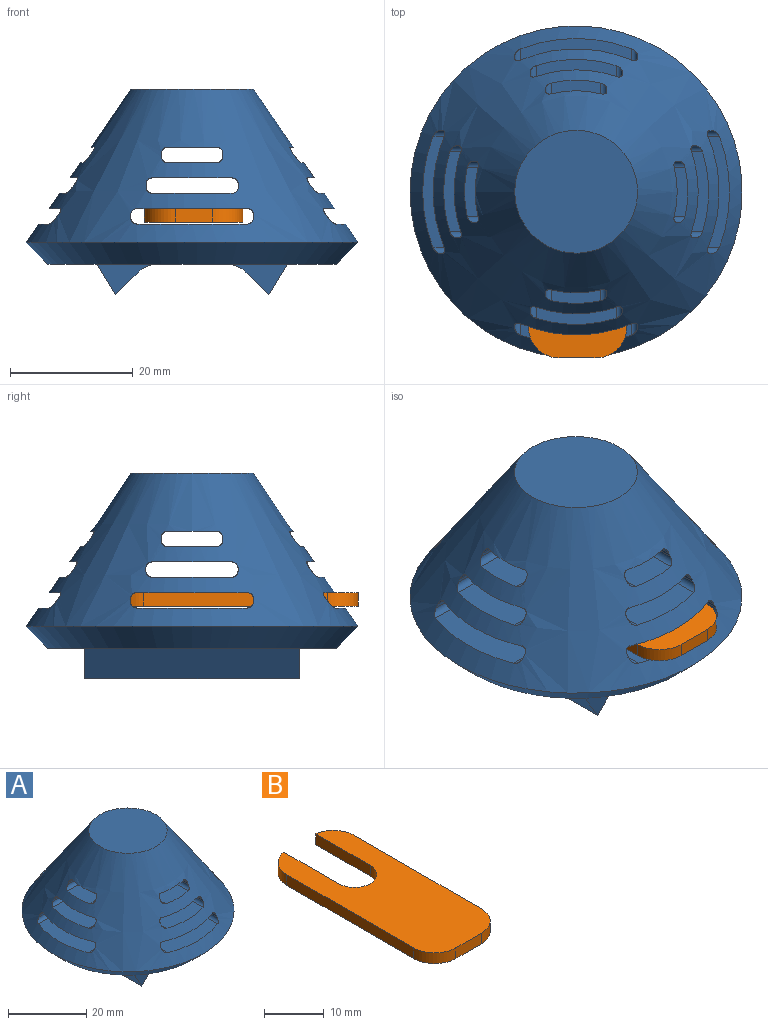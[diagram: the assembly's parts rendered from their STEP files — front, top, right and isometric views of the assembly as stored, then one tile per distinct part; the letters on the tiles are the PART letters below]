
ASSEMBLY  parts=2 mates=1
PART A: 97 faces, bbox 54.1x54.1x33.5 mm
  f0: cone r=27.04mm half-angle=34.3deg, axis (0,0,-1), area 2971.5mm2, adj f1,f2,f3,f4,f5,f6,f7,f8
  f1: cylinder r=1mm len=12.4mm, axis (0,-1,0), area 18.3mm2, adj f0,f24,f30,f66
  f2: cylinder r=1mm len=13.72mm, axis (0,-1,0), area 20mm2, adj f0,f27,f30,f64
  f3: cylinder r=1mm len=13.72mm, axis (0,-1,0), area 20mm2, adj f0,f27,f31,f67
  f4: cylinder r=1mm len=12.4mm, axis (0,-1,0), area 18.3mm2, adj f0,f24,f31,f69
  f5: plane 11.75x0.5mm, normal (1,0,0), area 5.8mm2, adj f0,f25,f26,f62
  f6: plane 11.75x0.5mm, normal (-1,0,0), area 5.8mm2, adj f0,f28,f29,f72
  f7: cylinder r=1mm len=12.64mm, axis (0,-1,0), area 18.8mm2, adj f0,f33,f36,f93
  f8: plane 12x0.5mm, normal (1,0,0), area 5.9mm2, adj f0,f35,f37,f95
  f9: cylinder r=1mm len=14.07mm, axis (0,-1,0), area 20.5mm2, adj f0,f34,f36,f91
  f10: cylinder r=1mm len=14.07mm, axis (0,-1,0), area 20.5mm2, adj f0,f34,f39,f87
  f11: plane 12x0.5mm, normal (-1,0,0), area 5.9mm2, adj f0,f38,f40,f89
  f12: cylinder r=1mm len=12.64mm, axis (0,-1,0), area 18.8mm2, adj f0,f33,f39,f85
  f13: cylinder r=1mm len=12.78mm, axis (0,-1,0), area 19mm2, adj f0,f41,f44,f81
  f14: plane 12.15x0.5mm, normal (1,0,0), area 6mm2, adj f0,f43,f45,f83
  f15: cylinder r=1mm len=14.31mm, axis (0,-1,0), area 20.8mm2, adj f0,f42,f44,f79
  f16: cylinder r=1mm len=14.31mm, axis (0,-1,0), area 20.8mm2, adj f0,f42,f47,f75
  f17: plane 12.15x0.5mm, normal (-1,0,0), area 6mm2, adj f0,f46,f48,f77
  f18: cylinder r=1mm len=12.78mm, axis (0,-1,0), area 19mm2, adj f0,f41,f47,f73
  f19: cone r=5mm half-angle=2deg, axis (0,0,-1), area 197.3mm2, adj f24,f49
  f20: plane 47x47mm, normal (0,0,-1), area 951.4mm2, adj f21,f23,f51,f53,f54,f55,f57,f58
  f21: cone r=5mm half-angle=2deg, axis (0,0,-1), area 200.8mm2, adj f20,f42
  f22: plane 20x20mm, normal (0,0,1), area 314.2mm2, adj f0
  f23: cone r=23.5mm half-angle=45deg, axis (0,0,1), area 793.8mm2, adj f0,f20
  f24: plane 32.92x32.92mm, normal (0,0,-1), area 398.4mm2, adj f0,f1,f4,f19,f25,f29,f65,f66
  f25: cylinder r=1mm len=12.4mm, axis (0,-1,0), area 18.3mm2, adj f0,f5,f24,f65
  f26: cylinder r=1mm len=13.72mm, axis (0,-1,0), area 20mm2, adj f0,f5,f27,f63
  f27: plane 36.33x36.33mm, normal (0,0,1), area 451.1mm2, adj f0,f2,f3,f26,f28,f32,f63,f64
  f28: cylinder r=1mm len=13.72mm, axis (0,-1,0), area 20mm2, adj f0,f6,f27,f68
  f29: cylinder r=1mm len=12.4mm, axis (0,-1,0), area 18.3mm2, adj f0,f6,f24,f70
  f30: plane 11.75x0.5mm, normal (1,0,0), area 5.8mm2, adj f0,f1,f2,f61
  f31: plane 11.75x0.5mm, normal (-1,0,0), area 5.8mm2, adj f0,f3,f4,f71
  f32: cone r=5mm half-angle=2deg, axis (0,0,-1), area 70.2mm2, adj f27,f33
  f33: plane 39.74x39.74mm, normal (0,0,-1), area 781.6mm2, adj f0,f7,f12,f32,f35,f40,f85,f88
  f34: plane 43.15x43.15mm, normal (0,0,1), area 869.4mm2, adj f0,f9,f10,f37,f38,f50,f87,f90
  f35: cylinder r=1mm len=12.64mm, axis (0,-1,0), area 18.8mm2, adj f0,f8,f33,f96
  f36: plane 12x0.5mm, normal (1,0,0), area 5.9mm2, adj f0,f7,f9,f94
  f37: cylinder r=1mm len=14.07mm, axis (0,-1,0), area 20.5mm2, adj f0,f8,f34,f92
  f38: cylinder r=1mm len=14.07mm, axis (0,-1,0), area 20.5mm2, adj f0,f11,f34,f90
  f39: plane 12x0.5mm, normal (-1,0,0), area 5.9mm2, adj f0,f10,f12,f86
  f40: cylinder r=1mm len=12.64mm, axis (0,-1,0), area 18.8mm2, adj f0,f11,f33,f88
  f41: plane 46.56x46.56mm, normal (0,0,-1), area 1240.7mm2, adj f0,f13,f18,f43,f48,f50,f73,f76
  f42: plane 49.98x49.98mm, normal (0,0,1), area 1363.9mm2, adj f0,f15,f16,f21,f45,f46,f75,f78
  f43: cylinder r=1mm len=12.78mm, axis (0,-1,0), area 19mm2, adj f0,f14,f41,f84
  f44: plane 12.15x0.5mm, normal (1,0,0), area 6mm2, adj f0,f13,f15,f82
  f45: cylinder r=1mm len=14.31mm, axis (0,-1,0), area 20.8mm2, adj f0,f14,f42,f80
  f46: cylinder r=1mm len=14.31mm, axis (0,-1,0), area 20.8mm2, adj f0,f17,f42,f78
  f47: plane 12.15x0.5mm, normal (-1,0,0), area 6mm2, adj f0,f16,f18,f74
  f48: cylinder r=1mm len=12.78mm, axis (0,-1,0), area 19mm2, adj f0,f17,f41,f76
  f49: plane 8.15x8.15mm, normal (0,0,-1), area 52.2mm2, adj f19
  f50: cone r=5mm half-angle=2deg, axis (0,0,-1), area 72.9mm2, adj f34,f41
  f51: plane 35x5mm, normal (-0.86,0,-0.51), area 204.1mm2, adj f20,f52,f53,f54
  f52: plane 35x3.54mm, normal (0.71,0,-0.71), area 175mm2, adj f51,f53,f54,f60
  f53: plane 10.07x5mm, normal (0,-1,0), area 20.5mm2, adj f20,f51,f52,f60
  f54: plane 10.07x5mm, normal (0,1,0), area 20.5mm2, adj f20,f51,f52,f60
  f55: plane 35x5mm, normal (0.86,0,-0.51), area 204.1mm2, adj f20,f56,f57,f58
  f56: plane 35x3.54mm, normal (-0.71,0,-0.71), area 175mm2, adj f55,f57,f58,f59
  f57: plane 10.07x5mm, normal (0,-1,0), area 20.5mm2, adj f20,f55,f56,f59
  f58: plane 10.07x5mm, normal (0,1,0), area 20.5mm2, adj f20,f55,f56,f59
  f59: cylinder r=5mm len=35mm, axis (0,-1,0), area 137.4mm2, adj f20,f56,f57,f58
  f60: cylinder r=5mm len=35mm, axis (0,1,0), area 137.4mm2, adj f20,f52,f53,f54
  f61: plane 11.75x0.5mm, normal (0,1,0), area 5.8mm2, adj f0,f30,f64,f66
  f62: plane 11.75x0.5mm, normal (0,-1,0), area 5.8mm2, adj f0,f5,f63,f65
  f63: cylinder r=1mm len=13.72mm, axis (1,0,0), area 20mm2, adj f0,f26,f27,f62
  f64: cylinder r=1mm len=13.72mm, axis (1,0,0), area 20mm2, adj f0,f2,f27,f61
  f65: cylinder r=1mm len=12.4mm, axis (1,0,0), area 18.3mm2, adj f0,f24,f25,f62
  f66: cylinder r=1mm len=12.4mm, axis (1,0,0), area 18.3mm2, adj f0,f1,f24,f61
  f67: cylinder r=1mm len=13.72mm, axis (1,0,0), area 20mm2, adj f0,f3,f27,f71
  f68: cylinder r=1mm len=13.72mm, axis (1,0,0), area 20mm2, adj f0,f27,f28,f72
  f69: cylinder r=1mm len=12.4mm, axis (1,0,0), area 18.3mm2, adj f0,f4,f24,f71
  f70: cylinder r=1mm len=12.4mm, axis (1,0,0), area 18.3mm2, adj f0,f24,f29,f72
  f71: plane 11.75x0.5mm, normal (0,1,0), area 5.8mm2, adj f0,f31,f67,f69
  f72: plane 11.75x0.5mm, normal (0,-1,0), area 5.8mm2, adj f0,f6,f68,f70
  f73: cylinder r=1mm len=12.78mm, axis (1,0,0), area 19mm2, adj f0,f18,f41,f74
  f74: plane 12.15x0.5mm, normal (0,1,0), area 6mm2, adj f0,f47,f73,f75
  f75: cylinder r=1mm len=14.31mm, axis (1,0,0), area 20.8mm2, adj f0,f16,f42,f74
  f76: cylinder r=1mm len=12.78mm, axis (1,0,0), area 19mm2, adj f0,f41,f48,f77
  f77: plane 12.15x0.5mm, normal (0,-1,0), area 6mm2, adj f0,f17,f76,f78
  f78: cylinder r=1mm len=14.31mm, axis (1,0,0), area 20.8mm2, adj f0,f42,f46,f77
  f79: cylinder r=1mm len=14.31mm, axis (1,0,0), area 20.8mm2, adj f0,f15,f42,f82
  f80: cylinder r=1mm len=14.31mm, axis (1,0,0), area 20.8mm2, adj f0,f42,f45,f83
  f81: cylinder r=1mm len=12.78mm, axis (1,0,0), area 19mm2, adj f0,f13,f41,f82
  f82: plane 12.15x0.5mm, normal (0,1,0), area 6mm2, adj f0,f44,f79,f81
  f83: plane 12.15x0.5mm, normal (0,-1,0), area 6mm2, adj f0,f14,f80,f84
  f84: cylinder r=1mm len=12.78mm, axis (1,0,0), area 19mm2, adj f0,f41,f43,f83
  f85: cylinder r=1mm len=12.64mm, axis (1,0,0), area 18.8mm2, adj f0,f12,f33,f86
  f86: plane 12x0.5mm, normal (0,1,0), area 5.9mm2, adj f0,f39,f85,f87
  f87: cylinder r=1mm len=14.07mm, axis (1,0,0), area 20.5mm2, adj f0,f10,f34,f86
  f88: cylinder r=1mm len=12.64mm, axis (1,0,0), area 18.8mm2, adj f0,f33,f40,f89
  f89: plane 12x0.5mm, normal (0,-1,0), area 5.9mm2, adj f0,f11,f88,f90
  f90: cylinder r=1mm len=14.07mm, axis (1,0,0), area 20.5mm2, adj f0,f34,f38,f89
  f91: cylinder r=1mm len=14.07mm, axis (1,0,0), area 20.5mm2, adj f0,f9,f34,f94
  f92: cylinder r=1mm len=14.07mm, axis (1,0,0), area 20.5mm2, adj f0,f34,f37,f95
  f93: cylinder r=1mm len=12.64mm, axis (1,0,0), area 18.8mm2, adj f0,f7,f33,f94
  f94: plane 12x0.5mm, normal (0,1,0), area 5.9mm2, adj f0,f36,f91,f93
  f95: plane 12x0.5mm, normal (0,-1,0), area 5.9mm2, adj f0,f8,f92,f96
  f96: cylinder r=1mm len=12.64mm, axis (1,0,0), area 18.8mm2, adj f0,f33,f35,f95
PART B: 12 faces, bbox 16x39.9x2.2 mm
  f0: cylinder r=5mm len=4.94mm, axis (0,0,-1), area 15.6mm2, adj f2,f3,f9,f10
  f1: cylinder r=3.75mm len=7.5mm, axis (0,0,-1), area 25.9mm2, adj f2,f9,f10,f11
  f2: plane 39.94x16mm, normal (0,0,-1), area 499mm2, adj f0,f1,f3,f4,f5,f6,f7,f8
  f3: plane 30x2.2mm, normal (1,0,0), area 66mm2, adj f0,f2,f8,f9
  f4: cylinder r=5mm len=4.94mm, axis (0,0,-1), area 15.6mm2, adj f2,f5,f9,f11
  f5: plane 30x2.2mm, normal (-1,0,0), area 66mm2, adj f2,f4,f6,f9
  f6: cylinder r=5mm len=5mm, axis (0,0,-1), area 17.3mm2, adj f2,f5,f7,f9
  f7: plane 6x2.2mm, normal (0,-1,0), area 13.2mm2, adj f2,f6,f8,f9
  f8: cylinder r=5mm len=5mm, axis (0,0,-1), area 17.3mm2, adj f2,f3,f7,f9
  f9: plane 39.94x16mm, normal (0,0,1), area 499mm2, adj f0,f1,f3,f4,f5,f6,f7,f8
  f10: plane 12.94x2.2mm, normal (-1,0,0), area 28.5mm2, adj f0,f1,f2,f9
  f11: plane 12.94x2.2mm, normal (1,0,0), area 28.5mm2, adj f1,f2,f4,f9
PLACE A t=(-0.22,-0.26,-26.62)mm
PLACE B t=(0.01,-7.29,-14.78)mm
MATE planar B.f9 <-> A.f0  axis (0,0,1) through (0.01,-10.17,-12.58)mm
